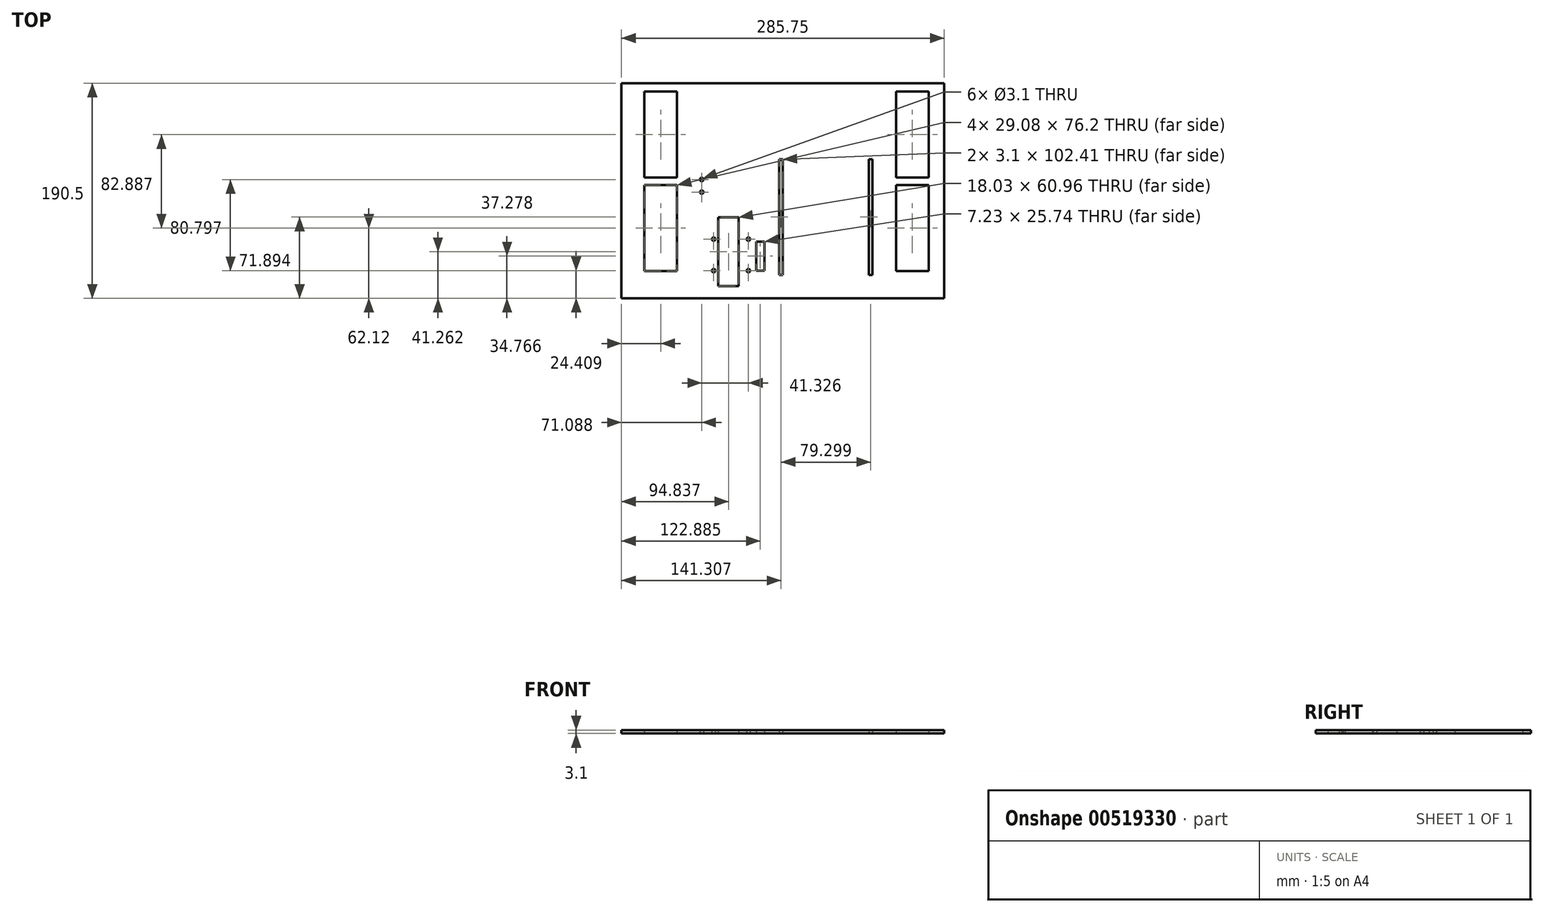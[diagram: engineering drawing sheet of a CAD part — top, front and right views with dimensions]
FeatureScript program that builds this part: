
annotation { "Feature Type Name" : "Feature", "Feature Type Description" : "" }
export const myFeature = defineFeature(function(context is Context, id is Id, definition is map)
    precondition{}
    {
        {
            var Q0;
            Q0=qCreatedBy(makeId("Top.planeOp"),FACE);
            var sketch = newSketch(context, id + "F0", { "sketchPlane" : qUnion([Q0])});
            skLineSegment(sketch, "E0.bottom", {"start": v(-181.56, 0) * mm, "end": v(104.2, 0) * mm});
            skLineSegment(sketch, "E0.top", {"start": v(-181.56, -190.5) * mm, "end": v(104.2, -190.5) * mm});
            skLineSegment(sketch, "E0.left", {"start": v(-181.56, 0) * mm, "end": v(-181.56, -190.5) * mm});
            skLineSegment(sketch, "E0.right", {"start": v(104.2, 0) * mm, "end": v(104.2, -190.5) * mm});
            skLineSegment(sketch, "E1.bottom", {"start": v(-95.74, -179.72) * mm, "end": v(-77.7, -179.72) * mm});
            skLineSegment(sketch, "E1.top", {"start": v(-95.74, -118.76) * mm, "end": v(-77.7, -118.76) * mm});
            skLineSegment(sketch, "E1.left", {"start": v(-77.7, -179.72) * mm, "end": v(-77.7, -118.76) * mm});
            skLineSegment(sketch, "E1.right", {"start": v(-95.74, -179.72) * mm, "end": v(-95.74, -118.76) * mm});
            skLineSegment(sketch, "E2.bottom", {"start": v(-41.8, -169.81) * mm, "end": v(-38.7, -169.81) * mm});
            skLineSegment(sketch, "E2.top", {"start": v(-41.8, -67.4) * mm, "end": v(-38.7, -67.4) * mm});
            skLineSegment(sketch, "E2.left", {"start": v(-41.8, -169.81) * mm, "end": v(-41.8, -67.4) * mm});
            skLineSegment(sketch, "E2.right", {"start": v(-38.7, -169.81) * mm, "end": v(-38.7, -67.4) * mm});
            skLineSegment(sketch, "E3.bottom", {"start": v(37.5, -169.81) * mm, "end": v(40.6, -169.81) * mm});
            skLineSegment(sketch, "E3.top", {"start": v(37.5, -67.4) * mm, "end": v(40.6, -67.4) * mm});
            skLineSegment(sketch, "E3.left", {"start": v(37.5, -169.81) * mm, "end": v(37.5, -67.4) * mm});
            skLineSegment(sketch, "E3.right", {"start": v(40.6, -169.81) * mm, "end": v(40.6, -67.4) * mm});
            skSolve(sketch);
        }
        {
            var Q0;
            Q0=makeQuery(id+"F0.imprint","IMPRINT",FACE,{"disambiguationData":[TD([[makeQuery(id+"F0.imprint","IMPRINT",EDGE,{"derivedFrom":sQuery(id+"F0.wireOp",EDGE,"E0.bottom")}),-1.0]])]});
            var sketch = newSketch(context, id + "F1", { "sketchPlane" : qUnion([Q0])});
            skCircle(sketch, "E4", {"center": v(-110.47, -85.3) * mm, "radius": 1.55 * mm});
            skCircle(sketch, "E5", {"center": v(-110.47, -96.5) * mm, "radius": 1.55 * mm});
            skCircle(sketch, "E6", {"center": v(-69.15, -138.15) * mm, "radius": 1.55 * mm});
            skCircle(sketch, "E7", {"center": v(-69.15, -166.1) * mm, "radius": 1.55 * mm});
            skCircle(sketch, "E8", {"center": v(-99.93, -166.1) * mm, "radius": 1.55 * mm});
            skCircle(sketch, "E9", {"center": v(-99.93, -138.15) * mm, "radius": 1.55 * mm});
            skLineSegment(sketch, "E10.bottom", {"start": v(-62.29, -166.1) * mm, "end": v(-55.06, -166.1) * mm});
            skLineSegment(sketch, "E10.top", {"start": v(-62.29, -140.35) * mm, "end": v(-55.06, -140.35) * mm});
            skLineSegment(sketch, "E10.left", {"start": v(-62.29, -166.1) * mm, "end": v(-62.29, -140.35) * mm});
            skLineSegment(sketch, "E10.right", {"start": v(-55.06, -166.1) * mm, "end": v(-55.06, -140.35) * mm});
            skLineSegment(sketch, "E11.bottom", {"start": v(-161.34, -166.48) * mm, "end": v(-132.25, -166.48) * mm});
            skLineSegment(sketch, "E11.top", {"start": v(-161.34, -90.28) * mm, "end": v(-132.25, -90.28) * mm});
            skLineSegment(sketch, "E11.left", {"start": v(-161.34, -166.48) * mm, "end": v(-161.34, -90.28) * mm});
            skLineSegment(sketch, "E11.right", {"start": v(-132.25, -166.48) * mm, "end": v(-132.25, -90.28) * mm});
            skLineSegment(sketch, "E12.bottom", {"start": v(-161.34, -83.6) * mm, "end": v(-132.25, -83.6) * mm});
            skLineSegment(sketch, "E12.top", {"start": v(-161.34, -7.4) * mm, "end": v(-132.25, -7.4) * mm});
            skLineSegment(sketch, "E12.left", {"start": v(-161.34, -83.6) * mm, "end": v(-161.34, -7.4) * mm});
            skLineSegment(sketch, "E12.right", {"start": v(-132.25, -83.6) * mm, "end": v(-132.25, -7.4) * mm});
            skLineSegment(sketch, "E13.bottom", {"start": v(61.43, -166.48) * mm, "end": v(90.52, -166.48) * mm});
            skLineSegment(sketch, "E13.top", {"start": v(61.43, -90.28) * mm, "end": v(90.52, -90.28) * mm});
            skLineSegment(sketch, "E13.left", {"start": v(61.43, -166.48) * mm, "end": v(61.43, -90.28) * mm});
            skLineSegment(sketch, "E13.right", {"start": v(90.52, -166.48) * mm, "end": v(90.52, -90.28) * mm});
            skLineSegment(sketch, "E14.bottom", {"start": v(61.43, -83.6) * mm, "end": v(90.52, -83.6) * mm});
            skLineSegment(sketch, "E14.top", {"start": v(61.43, -7.4) * mm, "end": v(90.52, -7.4) * mm});
            skLineSegment(sketch, "E14.left", {"start": v(61.43, -83.6) * mm, "end": v(61.43, -7.4) * mm});
            skLineSegment(sketch, "E14.right", {"start": v(90.52, -83.6) * mm, "end": v(90.52, -7.4) * mm});
            skSolve(sketch);
        }
        {
            var Q0;
            Q0=makeQuery(id+"F1.imprint","IMPRINT",FACE,{"disambiguationData":[TD([[makeQuery(id+"F1.imprint","IMPRINT",EDGE,{"derivedFrom":sQuery(id+"F1.wireOp",EDGE,"E4")}),-1.0]])]});
            extrude(context, id + "F2", {"entities" : qUnion([Q0]), "depth" : 3.1 * mm, "offsetDistance" : 25.4 * mm});
        }
    });
